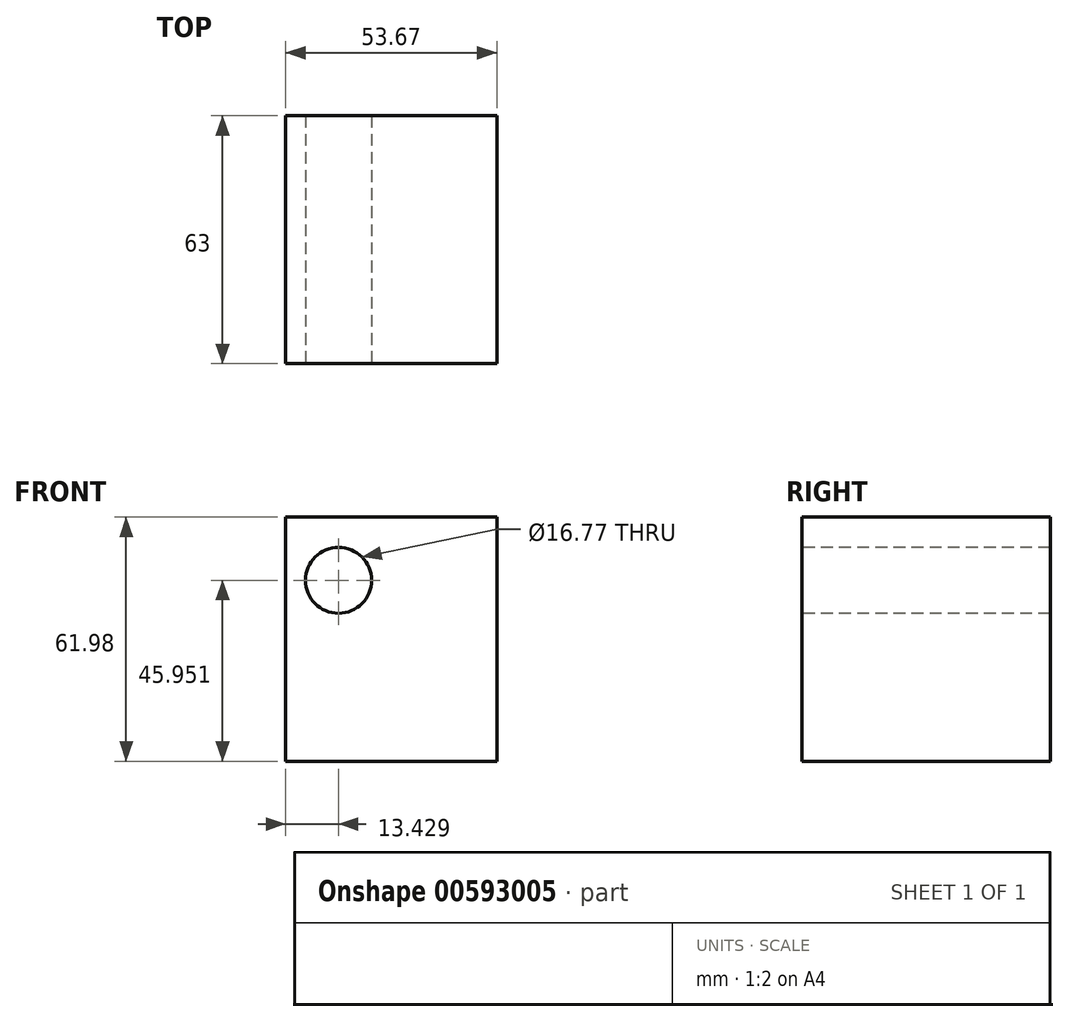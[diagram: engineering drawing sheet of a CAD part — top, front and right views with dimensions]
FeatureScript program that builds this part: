
annotation { "Feature Type Name" : "Feature", "Feature Type Description" : "" }
export const myFeature = defineFeature(function(context is Context, id is Id, definition is map)
    precondition{}
    {
        {
            var Q0;
            Q0=qCreatedBy(makeId("Front.planeOp"),FACE);
            var sketch = newSketch(context, id + "F0", { "sketchPlane" : qUnion([Q0])});
            skLineSegment(sketch, "E0.bottom", {"start": v(0, 0) * mm, "end": v(53.67, 0) * mm});
            skLineSegment(sketch, "E0.top", {"start": v(0, 61.98) * mm, "end": v(53.67, 61.98) * mm});
            skLineSegment(sketch, "E0.left", {"start": v(0, 0) * mm, "end": v(0, 61.98) * mm});
            skLineSegment(sketch, "E0.right", {"start": v(53.67, 0) * mm, "end": v(53.67, 61.98) * mm});
            skSolve(sketch);
        }
        {
            var Q0;
            Q0=makeQuery(id+"F0.imprint","IMPRINT",FACE,{"disambiguationData":[TD([[makeQuery(id+"F0.imprint","IMPRINT",EDGE,{"derivedFrom":sQuery(id+"F0.wireOp",EDGE,"E0.bottom")}),1.0]])]});
            extrude(context, id + "F1", {"entities" : qUnion([Q0]), "depth" : 63 * mm, "offsetDistance" : 25 * mm});
        }
        {
            var Q0;
            Q0=makeQuery(id+"F1.opExtrude","CAP_FACE",FACE,{"disambiguationData":[OSD([sQuery(id+"F0.wireOp",EDGE,"E0.bottom"),sQuery(id+"F0.wireOp",EDGE,"E0.top"),sQuery(id+"F0.wireOp",EDGE,"E0.left"),sQuery(id+"F0.wireOp",EDGE,"E0.right")])],"isStart":false});
            var sketch = newSketch(context, id + "F2", { "sketchPlane" : qUnion([Q0])});
            skCircle(sketch, "E1", {"center": v(13.43, 45.95) * mm, "radius": 8.38 * mm});
            skSolve(sketch);
        }
        {
            var Q0;
            Q0=makeQuery(id+"F2.imprint","IMPRINT",FACE,{"disambiguationData":[TD([[makeQuery(id+"F2.imprint","IMPRINT",EDGE,{"derivedFrom":sQuery(id+"F2.wireOp",EDGE,"E1")}),1.0]])]});
            extrude(context, id + "F3", {"entities" : qUnion([Q0]), "operationType" : NewBodyOperationType.REMOVE, "endBound" : BoundingType.THROUGH_ALL, "oppositeDirection" : true, "depth" : 25 * mm, "offsetDistance" : 25 * mm});
        }
    });
